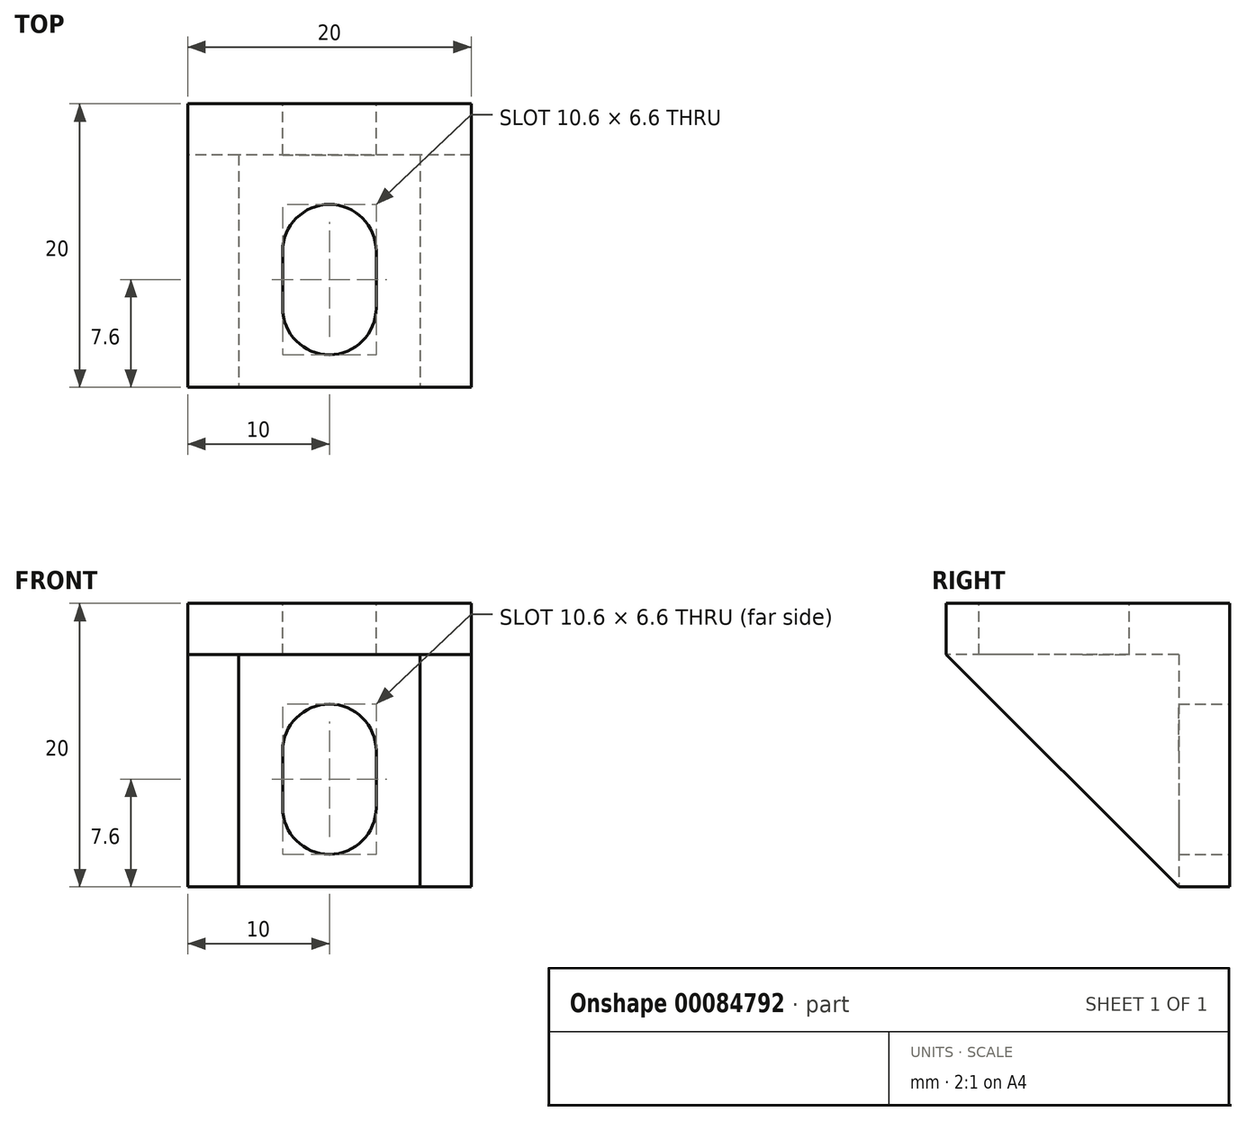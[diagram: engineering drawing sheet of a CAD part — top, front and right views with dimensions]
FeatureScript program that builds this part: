
annotation { "Feature Type Name" : "Feature", "Feature Type Description" : "" }
export const myFeature = defineFeature(function(context is Context, id is Id, definition is map)
    precondition{}
    {
        {
            var Q0;
            Q0=qCreatedBy(makeId("Top.planeOp"),FACE);
            var sketch = newSketch(context, id + "F0", { "sketchPlane" : qUnion([Q0])});
            skLineSegment(sketch, "E0.rect.bottom", {"start": v(10, 24) * mm, "end": v(-10, 24) * mm});
            skLineSegment(sketch, "E0.rect.left", {"start": v(10, 24) * mm, "end": v(10, 4) * mm});
            skLineSegment(sketch, "E0.rect.right", {"start": v(-10, 24) * mm, "end": v(-10, 4) * mm});
            skPoint(sketch, "E0.rect.middle", {"position": v(0, 0) * mm});
            skLineSegment(sketch, "E1", {"start": v(10, 4) * mm, "end": v(-10, 4) * mm});
            skPoint(sketch, "E0.rect.top.end.orphan", {"position": v(-10, -24) * mm});
            skPoint(sketch, "E0.rect.top.start.orphan", {"position": v(10, -24) * mm});
            skSolve(sketch);
        }
        {
            var Q0;
            Q0=makeQuery(id+"F0.imprint","IMPRINT",FACE,{"disambiguationData":[TD([[makeQuery(id+"F0.imprint","IMPRINT",EDGE,{"derivedFrom":sQuery(id+"F0.wireOp",EDGE,"E0.rect.bottom")}),1.0]])]});
            extrude(context, id + "F1", {"entities" : qUnion([Q0]), "depth" : 3.6 * mm});
        }
        {
            var Q0;
            Q0=makeQuery(id+"F1.opExtrude","CAP_FACE",FACE,{"disambiguationData":[OSD([sQuery(id+"F0.wireOp",EDGE,"E0.rect.bottom"),sQuery(id+"F0.wireOp",EDGE,"E0.rect.top"),sQuery(id+"F0.wireOp",EDGE,"E0.rect.left"),sQuery(id+"F0.wireOp",EDGE,"E0.rect.right")])],"isStart":false});
            var sketch = newSketch(context, id + "F2", { "sketchPlane" : qUnion([Q0])});
            skLineSegment(sketch, "E2.rect.bottom", {"start": v(-3.3, 13.6) * mm, "end": v(3.3, 13.6) * mm});
            skLineSegment(sketch, "E2.rect.top", {"start": v(-3.3, 9.6) * mm, "end": v(3.3, 9.6) * mm});
            skLineSegment(sketch, "E2.rect.left", {"start": v(-3.3, 13.6) * mm, "end": v(-3.3, 9.6) * mm});
            skLineSegment(sketch, "E2.rect.right", {"start": v(3.3, 13.6) * mm, "end": v(3.3, 9.6) * mm});
            skPoint(sketch, "E2.rect.middle", {"position": v(0, 0) * mm});
            skArc(sketch, "E3", {"start": v(-3.3, 9.6) * mm, "mid": v(0, 6.3) * mm, "end": v(3.3, 9.6) * mm});
            skArc(sketch, "E4", {"start": v(3.3, 13.6) * mm, "mid": v(0, 16.9) * mm, "end": v(-3.3, 13.6) * mm});
            skSolve(sketch);
        }
        {
            var Q0;
            Q0=qSketchRegion(id+"F2",true);
            extrude(context, id + "F3", {"entities" : qUnion([Q0]), "operationType" : NewBodyOperationType.REMOVE, "oppositeDirection" : true, "depth" : 25 * mm});
        }
        {
            var Q0;
            Q0=makeQuery(id+"F1.opExtrude","SWEPT_BODY",BODY,{"disambiguationData":[OSD([sQuery(id+"F0.wireOp",EDGE,"E0.rect.bottom"),sQuery(id+"F0.wireOp",EDGE,"E0.rect.left"),sQuery(id+"F0.wireOp",EDGE,"E0.rect.right"),sQuery(id+"F0.wireOp",EDGE,"E1")])]});
            var Q1;
            Q1=makeQuery(id+"F1.opExtrude","SWEPT_FACE",FACE,{"disambiguationData":[OSD([sQuery(id+"F0.wireOp",EDGE,"E0.rect.bottom")])]});
            mirror(context, id + "F4", {"entities" : qUnion([Q0]), "mirrorPlane" : qUnion([Q1])});
        }
        {
            var Q0;
            Q0=makeQuery(id+"F4.opPattern","COPY",BODY,{"derivedFrom":makeQuery(id+"F1.opExtrude","SWEPT_BODY",BODY,{"disambiguationData":[OSD([sQuery(id+"F0.wireOp",EDGE,"E0.rect.bottom"),sQuery(id+"F0.wireOp",EDGE,"E0.rect.left"),sQuery(id+"F0.wireOp",EDGE,"E0.rect.right"),sQuery(id+"F0.wireOp",EDGE,"E1")])]}),"instanceName":"1"});
            var Q1;
            Q1=makeQuery(id+"F1.opExtrude","CAP_EDGE",EDGE,{"disambiguationData":[OSD([sQuery(id+"F0.wireOp",EDGE,"E0.rect.bottom")])],"isStart":false});
            transform(context, id + "F5", {"entities" : qUnion([Q0]), "transformType" : TransformType.ROTATION, "transformAxis" : qUnion([Q1]), "angle" : 90 * degree, "makeCopy" : false});
        }
        {
            var Q0;
            Q0=makeQuery(id+"F1.opExtrude","SWEPT_BODY",BODY,{"disambiguationData":[OSD([sQuery(id+"F0.wireOp",EDGE,"E0.rect.bottom"),sQuery(id+"F0.wireOp",EDGE,"E0.rect.left"),sQuery(id+"F0.wireOp",EDGE,"E0.rect.right"),sQuery(id+"F0.wireOp",EDGE,"E1")])]});
            var Q1;
            Q1=makeQuery(id+"F4.opPattern","COPY",BODY,{"derivedFrom":makeQuery(id+"F1.opExtrude","SWEPT_BODY",BODY,{"disambiguationData":[OSD([sQuery(id+"F0.wireOp",EDGE,"E0.rect.bottom"),sQuery(id+"F0.wireOp",EDGE,"E0.rect.left"),sQuery(id+"F0.wireOp",EDGE,"E0.rect.right"),sQuery(id+"F0.wireOp",EDGE,"E1")])]}),"instanceName":"1"});
            booleanBodies(context, id + "F6", {"operationType" : BooleanOperationType.UNION, "tools" : qUnion([Q0, Q1])});
        }
        {
            var Q0;
            {var subQ0=makeQuery(id+"F1.opExtrude","SWEPT_FACE",FACE,{"disambiguationData":[OSD([sQuery(id+"F0.wireOp",EDGE,"E0.rect.left")])]});Q0=makeQuery(id+"F6.opBoolean","MERGE",FACE,{"derivedFrom":[subQ0,makeQuery(id+"F4.opPattern","COPY",FACE,{"derivedFrom":subQ0,"instanceName":"1"})]});}
            var sketch = newSketch(context, id + "F7", { "sketchPlane" : qUnion([Q0])});
            skLineSegment(sketch, "E5", {"start": v(4, 0) * mm, "end": v(20.4, -16.4) * mm});
            skSolve(sketch);
        }
        {
            var Q0;
            Q0=makeQuery(id+"F7.imprint","IMPRINT",FACE,{"disambiguationData":[TD([[makeQuery(id+"F7.imprint","IMPRINT",EDGE,{"derivedFrom":sQuery(id+"F7.wireOp",EDGE,"E5")}),1.0]])]});
            extrude(context, id + "F8", {"entities" : qUnion([Q0]), "operationType" : NewBodyOperationType.ADD, "oppositeDirection" : true, "depth" : 3.6 * mm, "offsetDistance" : 25 * mm});
        }
        {
            var Q0;
            {var subQ0=makeQuery(id+"F1.opExtrude","SWEPT_FACE",FACE,{"disambiguationData":[OSD([sQuery(id+"F0.wireOp",EDGE,"E0.rect.right")])]});Q0=makeQuery(id+"F6.opBoolean","MERGE",FACE,{"derivedFrom":[subQ0,makeQuery(id+"F4.opPattern","COPY",FACE,{"derivedFrom":subQ0,"instanceName":"1"})]});}
            var sketch = newSketch(context, id + "F9", { "sketchPlane" : qUnion([Q0])});
            skLineSegment(sketch, "E6", {"start": v(-4, 0) * mm, "end": v(-20.4, -16.4) * mm});
            skSolve(sketch);
        }
        {
            var Q0;
            Q0=makeQuery(id+"F9.imprint","IMPRINT",FACE,{"disambiguationData":[TD([[makeQuery(id+"F9.imprint","IMPRINT",EDGE,{"derivedFrom":sQuery(id+"F9.wireOp",EDGE,"E6")}),-1.0]])]});
            extrude(context, id + "F10", {"entities" : qUnion([Q0]), "operationType" : NewBodyOperationType.ADD, "oppositeDirection" : true, "depth" : 3.6 * mm, "offsetDistance" : 25 * mm});
        }
    });
